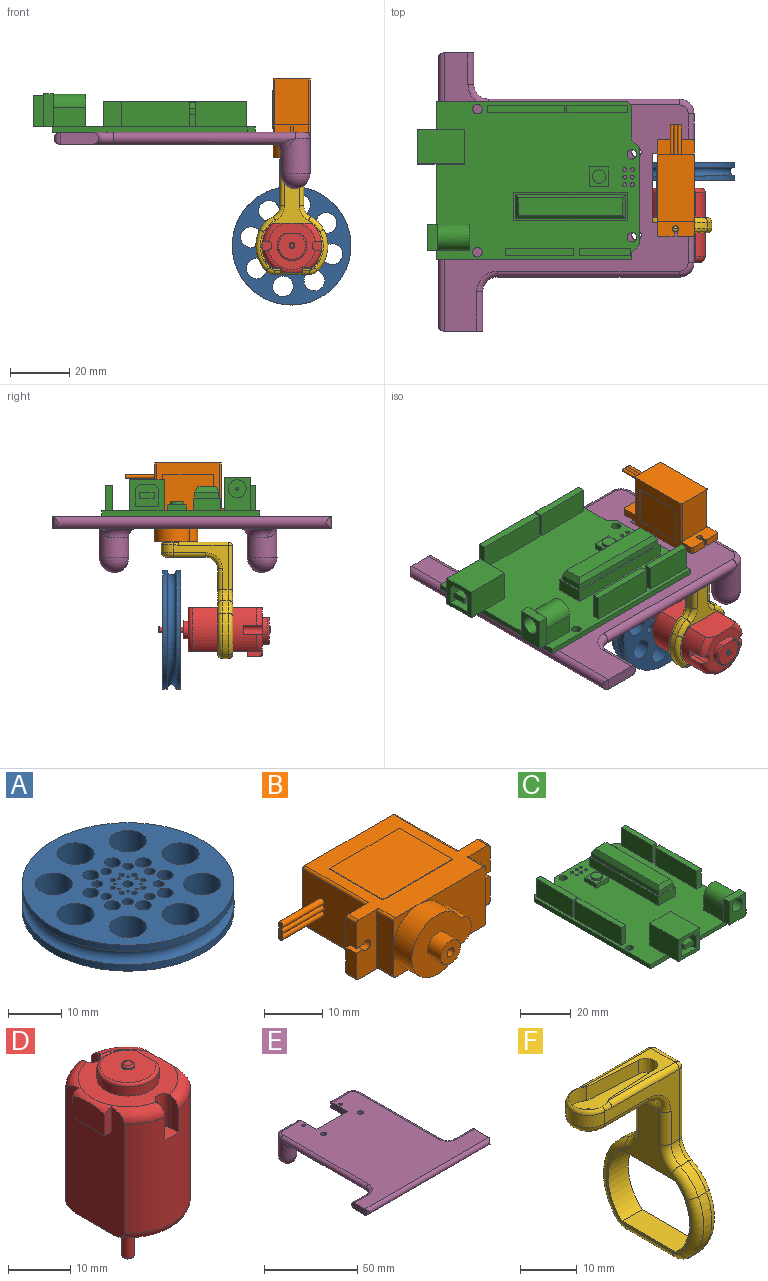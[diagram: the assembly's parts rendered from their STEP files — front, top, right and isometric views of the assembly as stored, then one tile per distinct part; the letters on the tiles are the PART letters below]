
ASSEMBLY  parts=6 mates=5
PART A: 46 faces, bbox 45.6x45.6x6 mm
  f0: cylinder r=20mm len=40mm, axis (0,0,-1), area 188.5mm2, adj f3,f45
  f1: cylinder r=20mm len=40mm, axis (0,0,-1), area 188.5mm2, adj f4,f45
  f2: cylinder r=1mm len=6mm, axis (0,0,-1), area 37.7mm2, adj f3,f4
  f3: plane 40x40mm, normal (0,0,1), area 856.1mm2, adj f0,f2,f5,f6,f7,f8,f9,f10
  f4: plane 40x40mm, normal (0,0,-1), area 856.1mm2, adj f1,f2,f5,f6,f7,f8,f9,f10
  f5: cylinder r=3.5mm len=7mm, axis (0,0,1), area 131.9mm2, adj f3,f4
  f6: cylinder r=3.5mm len=7mm, axis (0,0,1), area 131.9mm2, adj f3,f4
  f7: cylinder r=3.5mm len=7mm, axis (0,0,1), area 131.9mm2, adj f3,f4
  f8: cylinder r=3.5mm len=7mm, axis (0,0,1), area 131.9mm2, adj f3,f4
  f9: cylinder r=3.5mm len=7mm, axis (0,0,1), area 131.9mm2, adj f3,f4
  f10: cylinder r=3.5mm len=7mm, axis (0,0,1), area 131.9mm2, adj f3,f4
  f11: cylinder r=3.5mm len=7mm, axis (0,0,1), area 131.9mm2, adj f3,f4
  f12: cylinder r=3.5mm len=7mm, axis (0,0,1), area 131.9mm2, adj f3,f4
  f13: cylinder r=1.5mm len=6mm, axis (0,0,1), area 56.5mm2, adj f3,f4
  f14: cylinder r=0.5mm len=6mm, axis (0,0,1), area 18.8mm2, adj f3,f4
  f15: cylinder r=0.5mm len=6mm, axis (0,0,1), area 18.8mm2, adj f3,f4
  f16: cylinder r=0.5mm len=6mm, axis (0,0,1), area 18.8mm2, adj f3,f4
  f17: cylinder r=0.5mm len=6mm, axis (0,0,1), area 18.8mm2, adj f3,f4
  f18: cylinder r=0.5mm len=6mm, axis (0,0,1), area 18.8mm2, adj f3,f4
  f19: cylinder r=0.5mm len=6mm, axis (0,0,1), area 18.8mm2, adj f3,f4
  f20: cylinder r=0.5mm len=6mm, axis (0,0,1), area 18.8mm2, adj f3,f4
  f21: cylinder r=0.25mm len=6mm, axis (0,0,1), area 9.4mm2, adj f3,f4
  f22: cylinder r=0.25mm len=6mm, axis (0,0,1), area 9.4mm2, adj f3,f4
  f23: cylinder r=0.25mm len=6mm, axis (0,0,1), area 9.4mm2, adj f3,f4
  f24: cylinder r=0.25mm len=6mm, axis (0,0,1), area 9.4mm2, adj f3,f4
  f25: cylinder r=0.25mm len=6mm, axis (0,0,1), area 9.4mm2, adj f3,f4
  f26: cylinder r=0.25mm len=6mm, axis (0,0,1), area 9.4mm2, adj f3,f4
  f27: cylinder r=0.25mm len=6mm, axis (0,0,1), area 9.4mm2, adj f3,f4
  f28: cylinder r=0.25mm len=6mm, axis (0,0,1), area 9.4mm2, adj f3,f4
  f29: cylinder r=1.5mm len=6mm, axis (0,0,1), area 56.5mm2, adj f3,f4
  f30: cylinder r=1.5mm len=6mm, axis (0,0,1), area 56.5mm2, adj f3,f4
  f31: cylinder r=1.5mm len=6mm, axis (0,0,1), area 56.5mm2, adj f3,f4
  f32: cylinder r=1.5mm len=6mm, axis (0,0,1), area 56.5mm2, adj f3,f4
  f33: cylinder r=1.5mm len=6mm, axis (0,0,1), area 56.5mm2, adj f3,f4
  f34: cylinder r=1.5mm len=6mm, axis (0,0,1), area 56.5mm2, adj f3,f4
  f35: cylinder r=1.5mm len=6mm, axis (0,0,1), area 56.5mm2, adj f3,f4
  f36: cylinder r=1mm len=6mm, axis (0,0,1), area 37.7mm2, adj f3,f4
  f37: cylinder r=0.5mm len=6mm, axis (0,0,1), area 18.8mm2, adj f3,f4
  f38: cylinder r=1mm len=6mm, axis (0,0,1), area 37.7mm2, adj f3,f4
  f39: cylinder r=1mm len=6mm, axis (0,0,1), area 37.7mm2, adj f3,f4
  f40: cylinder r=1mm len=6mm, axis (0,0,1), area 37.7mm2, adj f3,f4
  f41: cylinder r=1mm len=6mm, axis (0,0,1), area 37.7mm2, adj f3,f4
  f42: cylinder r=1mm len=6mm, axis (0,0,1), area 37.7mm2, adj f3,f4
  f43: cylinder r=1mm len=6mm, axis (0,0,1), area 37.7mm2, adj f3,f4
  f44: cylinder r=1mm len=6mm, axis (0,0,1), area 37.7mm2, adj f3,f4
  f45: torus R=20mm, axis (0,0,1), area 563.9mm2, adj f0,f1
PART B: 59 faces, bbox 37.5x29.7x12.7 mm
  f0: plane 31.5x22mm, normal (0,0,-1), area 277mm2, adj f1,f3,f4,f15,f16,f17,f23,f25
  f1: cylinder r=0.5mm len=4mm, axis (0,-1,0), area 3.1mm2, adj f0,f3,f20,f23
  f2: plane 6.25x6.25mm, normal (0,-1,0), area 8.3mm2, adj f5,f7,f18,f47
  f3: plane 16.25x12.5mm, normal (0,-1,0), area 132.6mm2, adj f0,f1,f18,f20,f22,f47,f48
  f4: plane 6.25x6.25mm, normal (0,-1,0), area 8.3mm2, adj f0,f7,f34,f47
  f5: cylinder r=0.5mm len=4mm, axis (0,-1,0), area 3.1mm2, adj f2,f7,f18,f33
  f6: plane 15.5x11.5mm, normal (-1,0,0), area 174.9mm2, adj f8,f12,f13,f14,f15,f16,f17
  f7: plane 11.5x4mm, normal (-1,0,0), area 46mm2, adj f2,f4,f5,f33,f34
  f8: cylinder r=0.6mm len=10mm, axis (-1,0,0), area 37.7mm2, adj f6,f9
  f9: plane 1.2x1.2mm, normal (-1,0,0), area 1.1mm2, adj f8
  f10: plane 1.2x1.2mm, normal (-1,0,0), area 1.1mm2, adj f12
  f11: plane 1.2x1.2mm, normal (-1,0,0), area 1.1mm2, adj f13
  f12: cylinder r=0.6mm len=10mm, axis (-1,0,0), area 37.7mm2, adj f6,f10
  f13: cylinder r=0.6mm len=10mm, axis (-1,0,0), area 37.7mm2, adj f6,f11
  f14: cylinder r=0.5mm len=15.5mm, axis (0,-1,0), area 12.2mm2, adj f6,f15,f17,f18
  f15: plane 22.5x12.5mm, normal (0,1,0), area 281mm2, adj f0,f6,f14,f16,f18,f19,f21,f26
  f16: cylinder r=0.5mm len=15.5mm, axis (0,1,0), area 12.2mm2, adj f0,f6,f15,f17
  f17: plane 12.5x5.5mm, normal (0,1,0), area 57.8mm2, adj f0,f6,f14,f16,f18,f35,f36,f37
  f18: plane 31.5x22mm, normal (0,0,1), area 277mm2, adj f2,f3,f5,f14,f15,f17,f19,f22
  f19: cylinder r=0.5mm len=15.5mm, axis (0,1,0), area 12.2mm2, adj f15,f18,f21,f25
  f20: plane 11.5x4mm, normal (1,0,0), area 46mm2, adj f1,f3,f22,f23
  f21: plane 15.5x11.5mm, normal (1,0,0), area 178.2mm2, adj f15,f19,f25,f26
  f22: cylinder r=0.5mm len=4mm, axis (0,1,0), area 3.1mm2, adj f3,f18,f20,f23
  f23: plane 12.5x5.5mm, normal (0,-1,0), area 57.8mm2, adj f0,f1,f18,f20,f22,f24,f27,f28
  f24: cylinder r=0.5mm len=2.5mm, axis (0,1,0), area 2mm2, adj f18,f23,f25,f28
  f25: plane 12.5x5.5mm, normal (0,1,0), area 57.8mm2, adj f0,f18,f19,f21,f24,f26,f27,f28
  f26: cylinder r=0.5mm len=15.5mm, axis (0,-1,0), area 12.2mm2, adj f0,f15,f21,f25
  f27: cylinder r=0.5mm len=2.5mm, axis (0,-1,0), area 2mm2, adj f0,f23,f25,f29
  f28: plane 5.25x2.5mm, normal (1,0,0), area 13.1mm2, adj f23,f24,f25,f30
  f29: plane 5.25x2.5mm, normal (1,0,0), area 13.1mm2, adj f23,f25,f27,f32
  f30: plane 2.5x1.63mm, normal (0,0,-1), area 4.1mm2, adj f23,f25,f28,f31
  f31: cylinder r=1mm len=2.5mm, axis (0,-1,0), area 13.1mm2, adj f23,f25,f30,f32
  f32: plane 2.5x1.63mm, normal (0,0,1), area 4.1mm2, adj f23,f25,f29,f31
  f33: plane 12.5x5.5mm, normal (0,-1,0), area 57.8mm2, adj f0,f5,f7,f18,f34,f35,f36,f37
  f34: cylinder r=0.5mm len=4mm, axis (0,1,0), area 3.1mm2, adj f0,f4,f7,f33
  f35: cylinder r=0.5mm len=2.5mm, axis (0,1,0), area 2mm2, adj f0,f17,f33,f37
  f36: plane 5.25x2.5mm, normal (-1,0,0), area 13.1mm2, adj f17,f33,f38,f39
  f37: plane 5.25x2.5mm, normal (-1,0,0), area 13.1mm2, adj f17,f33,f35,f41
  f38: cylinder r=0.5mm len=2.5mm, axis (0,-1,0), area 2mm2, adj f17,f18,f33,f36
  f39: plane 2.5x1.63mm, normal (0,0,-1), area 4.1mm2, adj f17,f33,f36,f40
  f40: cylinder r=1mm len=2.5mm, axis (0,-1,0), area 13.1mm2, adj f17,f33,f39,f41
  f41: plane 2.5x1.63mm, normal (0,0,1), area 4.1mm2, adj f17,f33,f37,f40
  f42: plane 13x0.1mm, normal (-1,0,0), area 1.3mm2, adj f18,f43,f45,f46
  f43: plane 17x0.1mm, normal (0,1,0), area 1.7mm2, adj f18,f42,f44,f46
  f44: plane 13x0.1mm, normal (1,0,0), area 1.3mm2, adj f18,f43,f45,f46
  f45: plane 17x0.1mm, normal (0,-1,0), area 1.7mm2, adj f18,f42,f44,f46
  f46: plane 17x13mm, normal (0,0,1), area 221mm2, adj f42,f43,f44,f45
  f47: cylinder r=6.25mm len=12.5mm, axis (0,-1,0), area 150.6mm2, adj f2,f3,f4,f48,f49
  f48: cylinder r=2.8mm len=5.59mm, axis (0,-1,0), area 38.3mm2, adj f3,f47,f49
  f49: plane 14.5x12.5mm, normal (0,-1,0), area 113.7mm2, adj f47,f48,f51
  f50: plane 1.7x1.7mm, normal (0,-1,0), area 2.3mm2, adj f53
  f51: cylinder r=2.4mm len=4.8mm, axis (0,-1,0), area 48.3mm2, adj f49,f52
  f52: plane 4.8x4.8mm, normal (0,-1,0), area 15.8mm2, adj f51,f53
  f53: cylinder r=0.85mm len=3.2mm, axis (0,-1,0), area 17.1mm2, adj f50,f52
  f54: plane 13x0.1mm, normal (-1,0,0), area 1.3mm2, adj f0,f55,f56,f57
  f55: plane 17x0.1mm, normal (0,1,0), area 1.7mm2, adj f0,f54,f56,f58
  f56: plane 17x13mm, normal (0,0,-1), area 221mm2, adj f54,f55,f57,f58
  f57: plane 17x0.1mm, normal (0,-1,0), area 1.7mm2, adj f0,f54,f56,f58
  f58: plane 13x0.1mm, normal (1,0,0), area 1.3mm2, adj f0,f55,f56,f57
PART C: 159 faces, bbox 53.3x75x13 mm
  f0: plane 68.58x53.34mm, normal (0,0,1), area 2744.3mm2, adj f1,f2,f3,f4,f5,f6,f7,f8
  f1: plane 2.54x2.54mm, normal (0.71,0.71,0), area 6.8mm2, adj f0,f2,f51,f52
  f2: plane 32.77x1.9mm, normal (0,1,0), area 62.3mm2, adj f0,f1,f3,f52
  f3: plane 2.54x2.54mm, normal (-0.71,0.71,0), area 6.8mm2, adj f0,f2,f4,f52
  f4: plane 11.43x1.9mm, normal (0,1,0), area 21.7mm2, adj f0,f3,f5,f52
  f5: plane 1.9x1.52mm, normal (-0.71,0.71,0), area 4.1mm2, adj f0,f4,f6,f52
  f6: plane 64.52x1.9mm, normal (-1,0,0), area 122.6mm2, adj f0,f5,f7,f52
  f7: plane 53.34x1.9mm, normal (0,-1,0), area 101.3mm2, adj f0,f6,f8,f52,f81,f99,f107,f108
  f8: plane 66.04x1.9mm, normal (1,0,0), area 125.5mm2, adj f0,f7,f51,f52
  f9: cylinder r=1.59mm len=3.18mm, axis (0,0,-1), area 19mm2, adj f0,f52
  f10: cylinder r=1.59mm len=3.18mm, axis (0,0,-1), area 19mm2, adj f0,f52
  f11: cylinder r=1.59mm len=3.18mm, axis (0,0,-1), area 19mm2, adj f0,f52
  f12: cylinder r=1.59mm len=3.18mm, axis (0,0,-1), area 19mm2, adj f0,f52
  f13: cylinder r=0.64mm len=1.9mm, axis (0,0,-1), area 7.6mm2, adj f52,f80
  f14: cylinder r=0.64mm len=1.9mm, axis (0,0,-1), area 7.6mm2, adj f52,f79
  f15: cylinder r=0.64mm len=1.9mm, axis (0,0,-1), area 7.6mm2, adj f52,f78
  f16: cylinder r=0.64mm len=1.9mm, axis (0,0,-1), area 7.6mm2, adj f52,f77
  f17: cylinder r=0.64mm len=1.9mm, axis (0,0,-1), area 7.6mm2, adj f52,f76
  f18: cylinder r=0.64mm len=1.9mm, axis (0,0,-1), area 7.6mm2, adj f52,f75
  f19: cylinder r=0.64mm len=1.9mm, axis (0,0,-1), area 7.6mm2, adj f52,f74
  f20: cylinder r=0.64mm len=1.9mm, axis (0,0,-1), area 7.6mm2, adj f52,f73
  f21: cylinder r=0.64mm len=1.9mm, axis (0,0,-1), area 7.6mm2, adj f52,f72
  f22: cylinder r=0.64mm len=1.9mm, axis (0,0,-1), area 7.6mm2, adj f52,f71
  f23: cylinder r=0.64mm len=1.9mm, axis (0,0,-1), area 7.6mm2, adj f52,f58
  f24: cylinder r=0.64mm len=1.9mm, axis (0,0,-1), area 7.6mm2, adj f52,f140
  f25: cylinder r=0.64mm len=1.9mm, axis (0,0,-1), area 7.6mm2, adj f52,f151
  f26: cylinder r=0.64mm len=1.9mm, axis (0,0,-1), area 7.6mm2, adj f52,f59
  f27: cylinder r=0.64mm len=1.9mm, axis (0,0,-1), area 7.6mm2, adj f52,f60
  f28: cylinder r=0.64mm len=1.9mm, axis (0,0,-1), area 7.6mm2, adj f52,f61
  f29: cylinder r=0.64mm len=1.9mm, axis (0,0,-1), area 7.6mm2, adj f52,f62
  f30: cylinder r=0.64mm len=1.9mm, axis (0,0,-1), area 7.6mm2, adj f52,f63
  f31: cylinder r=0.64mm len=1.9mm, axis (0,0,-1), area 7.6mm2, adj f52,f64
  f32: cylinder r=0.64mm len=1.9mm, axis (0,0,-1), area 7.6mm2, adj f52,f65
  f33: cylinder r=0.64mm len=1.9mm, axis (0,0,-1), area 7.6mm2, adj f52,f139
  f34: cylinder r=0.64mm len=1.9mm, axis (0,0,-1), area 7.6mm2, adj f52,f138
  f35: cylinder r=0.64mm len=1.9mm, axis (0,0,-1), area 7.6mm2, adj f52,f137
  f36: cylinder r=0.64mm len=1.9mm, axis (0,0,-1), area 7.6mm2, adj f52,f136
  f37: cylinder r=0.64mm len=1.9mm, axis (0,0,-1), area 7.6mm2, adj f52,f135
  f38: cylinder r=0.64mm len=1.9mm, axis (0,0,-1), area 7.6mm2, adj f52,f134
  f39: cylinder r=0.64mm len=1.9mm, axis (0,0,-1), area 7.6mm2, adj f52,f133
  f40: cylinder r=0.64mm len=1.9mm, axis (0,0,-1), area 7.6mm2, adj f52,f150
  f41: cylinder r=0.64mm len=1.9mm, axis (0,0,-1), area 7.6mm2, adj f52,f149
  f42: cylinder r=0.64mm len=1.9mm, axis (0,0,-1), area 7.6mm2, adj f52,f148
  f43: cylinder r=0.64mm len=1.9mm, axis (0,0,-1), area 7.6mm2, adj f52,f147
  f44: cylinder r=0.64mm len=1.9mm, axis (0,0,-1), area 7.6mm2, adj f52,f146
  f45: cylinder r=0.64mm len=1.9mm, axis (0,0,-1), area 7.6mm2, adj f0,f52
  f46: cylinder r=0.64mm len=1.9mm, axis (0,0,-1), area 7.6mm2, adj f0,f52
  f47: cylinder r=0.64mm len=1.9mm, axis (0,0,-1), area 7.6mm2, adj f0,f52
  f48: cylinder r=0.64mm len=1.9mm, axis (0,0,-1), area 7.6mm2, adj f0,f52
  f49: cylinder r=0.64mm len=1.9mm, axis (0,0,-1), area 7.6mm2, adj f0,f52
  f50: cylinder r=0.64mm len=1.9mm, axis (0,0,-1), area 7.6mm2, adj f0,f52
  f51: plane 2.54x1.9mm, normal (0,1,0), area 4.8mm2, adj f0,f1,f8,f52
  f52: plane 68.58x53.34mm, normal (0,0,-1), area 3531.3mm2, adj f1,f2,f3,f4,f5,f6,f7,f8
  f53: plane 20.48x2.5mm, normal (0,0,1), area 51.2mm2, adj f54,f55,f56,f57
  f54: plane 8.6x2.5mm, normal (0,1,0), area 21.5mm2, adj f0,f53,f55,f57
  f55: plane 20.48x8.6mm, normal (1,0,0), area 176.1mm2, adj f0,f53,f54,f56
  f56: plane 8.6x2.5mm, normal (0,-1,0), area 21.5mm2, adj f0,f53,f55,f57
  f57: plane 20.48x8.6mm, normal (-1,0,0), area 176.1mm2, adj f0,f53,f54,f56
  f58: plane 1.27x1.27mm, normal (0,0,-1), area 1.3mm2, adj f23
  f59: plane 1.27x1.27mm, normal (0,0,-1), area 1.3mm2, adj f26
  f60: plane 1.27x1.27mm, normal (0,0,-1), area 1.3mm2, adj f27
  f61: plane 1.27x1.27mm, normal (0,0,-1), area 1.3mm2, adj f28
  f62: plane 1.27x1.27mm, normal (0,0,-1), area 1.3mm2, adj f29
  f63: plane 1.27x1.27mm, normal (0,0,-1), area 1.3mm2, adj f30
  f64: plane 1.27x1.27mm, normal (0,0,-1), area 1.3mm2, adj f31
  f65: plane 1.27x1.27mm, normal (0,0,-1), area 1.3mm2, adj f32
  f66: plane 26x2.5mm, normal (0,0,1), area 65mm2, adj f67,f68,f69,f70
  f67: plane 26x8.6mm, normal (1,0,0), area 223.6mm2, adj f0,f66,f68,f70
  f68: plane 8.6x2.5mm, normal (0,-1,0), area 21.5mm2, adj f0,f66,f67,f69
  f69: plane 26x8.6mm, normal (-1,0,0), area 223.6mm2, adj f0,f66,f68,f70
  f70: plane 8.6x2.5mm, normal (0,1,0), area 21.5mm2, adj f0,f66,f67,f69
  f71: plane 1.27x1.27mm, normal (0,0,-1), area 1.3mm2, adj f22
  f72: plane 1.27x1.27mm, normal (0,0,-1), area 1.3mm2, adj f21
  f73: plane 1.27x1.27mm, normal (0,0,-1), area 1.3mm2, adj f20
  f74: plane 1.27x1.27mm, normal (0,0,-1), area 1.3mm2, adj f19
  f75: plane 1.27x1.27mm, normal (0,0,-1), area 1.3mm2, adj f18
  f76: plane 1.27x1.27mm, normal (0,0,-1), area 1.3mm2, adj f17
  f77: plane 1.27x1.27mm, normal (0,0,-1), area 1.3mm2, adj f16
  f78: plane 1.27x1.27mm, normal (0,0,-1), area 1.3mm2, adj f15
  f79: plane 1.27x1.27mm, normal (0,0,-1), area 1.3mm2, adj f14
  f80: plane 1.27x1.27mm, normal (0,0,-1), area 1.3mm2, adj f13
  f81: plane 11.6x6.38mm, normal (0,0,-1), area 73.9mm2, adj f7,f82,f83,f85
  f82: plane 11.6x10.5mm, normal (0,-1,0), area 64.6mm2, adj f81,f83,f85,f86,f87,f88,f89,f90
  f83: plane 16x10.5mm, normal (1,0,0), area 168mm2, adj f0,f81,f82,f84,f86
  f84: plane 11.6x10.5mm, normal (0,1,0), area 121.8mm2, adj f0,f83,f85,f86
  f85: plane 16x10.5mm, normal (-1,0,0), area 168mm2, adj f0,f81,f82,f84,f86
  f86: plane 16x11.6mm, normal (0,0,1), area 185.6mm2, adj f82,f83,f84,f85
  f87: plane 14.14x5.02mm, normal (0,0,-1), area 71mm2, adj f82,f88,f92,f93
  f88: plane 14.14x1.44mm, normal (0.71,0,-0.71), area 28.8mm2, adj f82,f87,f89,f93
  f89: plane 14.14x6.06mm, normal (1,0,0), area 85.7mm2, adj f82,f88,f90,f93
  f90: plane 14.14x7.9mm, normal (0,0,1), area 111.7mm2, adj f82,f89,f91,f93
  f91: plane 14.14x6.06mm, normal (-1,0,0), area 85.7mm2, adj f82,f90,f92,f93
  f92: plane 14.14x1.44mm, normal (-0.71,0,-0.71), area 28.8mm2, adj f82,f87,f91,f93
  f93: plane 7.9x7.5mm, normal (0,-1,0), area 47mm2, adj f87,f88,f89,f90,f91,f92,f95,f96
  f94: plane 4.88x2.08mm, normal (0,-1,0), area 10.2mm2, adj f95,f96,f97,f98
  f95: plane 14.14x4.88mm, normal (0,0,1), area 69mm2, adj f93,f94,f96,f98
  f96: plane 14.14x2.08mm, normal (-1,0,0), area 29.4mm2, adj f93,f94,f95,f97
  f97: plane 14.14x4.88mm, normal (0,0,-1), area 69mm2, adj f93,f94,f96,f98
  f98: plane 14.14x2.08mm, normal (1,0,0), area 29.4mm2, adj f93,f94,f95,f97
  f99: plane 8.88x2.88mm, normal (0,0,-1), area 25.5mm2, adj f7,f107,f108,f109
  f100: plane 11x6.49mm, normal (1,0,0), area 71.4mm2, adj f0,f101,f103,f104
  f101: cylinder r=4.44mm len=11mm, axis (0,-1,0), area 153.4mm2, adj f100,f102,f103,f104,f105
  f102: plane 11x6.49mm, normal (-1,0,0), area 71.4mm2, adj f0,f101,f103,f105
  f103: plane 10.93x8.88mm, normal (0,1,0), area 88.6mm2, adj f0,f100,f101,f102
  f104: plane 6.63x0mm, normal (0,-1,0), area 0mm2, adj f0,f100,f101,f108
  f105: plane 11.12x8.88mm, normal (0,1,0), area 10.1mm2, adj f0,f101,f102,f106,f107,f108
  f106: plane 8.88x3.3mm, normal (0,0,1), area 29.3mm2, adj f105,f107,f108,f109
  f107: plane 11.13x3.3mm, normal (-1,0,0), area 36.7mm2, adj f0,f7,f99,f105,f106,f109
  f108: plane 11.13x3.3mm, normal (1,0,0), area 36.7mm2, adj f0,f7,f99,f104,f105,f106,f109
  f109: plane 11.13x8.88mm, normal (0,-1,0), area 70.5mm2, adj f99,f106,f107,f108,f110
  f110: cylinder r=3mm len=12.8mm, axis (0,-1,0), area 241.3mm2, adj f109,f111
  f111: plane 6x6mm, normal (0,-1,0), area 27.5mm2, adj f110,f112
  f112: cylinder r=0.5mm len=10mm, axis (0,1,0), area 31.4mm2, adj f111,f113
  f113: sphere r=0.5mm, area 1.6mm2, adj f112
  f114: plane 9.33x4.3mm, normal (0,-1,0), area 40.1mm2, adj f0,f115,f117,f118
  f115: plane 38.37x4.3mm, normal (1,0,0), area 164.8mm2, adj f0,f114,f116,f118
  f116: plane 9.33x4.3mm, normal (0,1,0), area 40.1mm2, adj f0,f115,f117,f118
  f117: plane 38.37x4.3mm, normal (-1,0,0), area 164.8mm2, adj f0,f114,f116,f118
  f118: plane 38.37x9.33mm, normal (0,0,1), area 57.4mm2, adj f114,f115,f116,f117,f119,f120,f121,f122
  f119: plane 37.19x2mm, normal (-1,0,0), area 74.4mm2, adj f118,f120,f122,f127
  f120: plane 8.08x2mm, normal (0,-1,0), area 16.2mm2, adj f118,f119,f121,f126
  f121: plane 37.19x2mm, normal (1,0,0), area 74.4mm2, adj f118,f120,f122,f125
  f122: plane 8.08x2mm, normal (0,1,0), area 16.2mm2, adj f118,f119,f121,f124
  f123: plane 35.16x6.05mm, normal (0,0,1), area 212.7mm2, adj f124,f125,f126,f127
  f124: plane 8.08x2mm, normal (0,0.9,0.44), area 15.7mm2, adj f122,f123,f125,f127
  f125: plane 37.19x2mm, normal (0.89,0,0.45), area 81.1mm2, adj f121,f123,f124,f126
  f126: plane 8.08x2mm, normal (0,-0.88,0.47), area 16mm2, adj f120,f123,f125,f127
  f127: plane 37.19x2mm, normal (-0.89,0,0.45), area 81.2mm2, adj f119,f123,f124,f126
  f128: plane 23x2.44mm, normal (0,0,1), area 56mm2, adj f129,f130,f131,f132
  f129: plane 23x8.6mm, normal (1,0,0), area 197.8mm2, adj f0,f128,f130,f132
  f130: plane 8.6x2.44mm, normal (0,-1,0), area 20.9mm2, adj f0,f128,f129,f131
  f131: plane 23x8.6mm, normal (-1,0,0), area 197.8mm2, adj f0,f128,f130,f132
  f132: plane 8.6x2.44mm, normal (0,1,0), area 20.9mm2, adj f0,f128,f129,f131
  f133: plane 1.27x1.27mm, normal (0,0,-1), area 1.3mm2, adj f39
  f134: plane 1.27x1.27mm, normal (0,0,-1), area 1.3mm2, adj f38
  f135: plane 1.27x1.27mm, normal (0,0,-1), area 1.3mm2, adj f37
  f136: plane 1.27x1.27mm, normal (0,0,-1), area 1.3mm2, adj f36
  f137: plane 1.27x1.27mm, normal (0,0,-1), area 1.3mm2, adj f35
  f138: plane 1.27x1.27mm, normal (0,0,-1), area 1.3mm2, adj f34
  f139: plane 1.27x1.27mm, normal (0,0,-1), area 1.3mm2, adj f33
  f140: plane 1.27x1.27mm, normal (0,0,-1), area 1.3mm2, adj f24
  f141: plane 17.27x2.44mm, normal (0,0,1), area 42.1mm2, adj f142,f143,f144,f145
  f142: plane 8.6x2.44mm, normal (0,-1,0), area 20.9mm2, adj f0,f141,f143,f145
  f143: plane 17.27x8.6mm, normal (-1,0,0), area 148.6mm2, adj f0,f141,f142,f144
  f144: plane 8.6x2.44mm, normal (0,1,0), area 20.9mm2, adj f0,f141,f143,f145
  f145: plane 17.27x8.6mm, normal (1,0,0), area 148.6mm2, adj f0,f141,f142,f144
  f146: plane 1.27x1.27mm, normal (0,0,-1), area 1.3mm2, adj f44
  f147: plane 1.27x1.27mm, normal (0,0,-1), area 1.3mm2, adj f43
  f148: plane 1.27x1.27mm, normal (0,0,-1), area 1.3mm2, adj f42
  f149: plane 1.27x1.27mm, normal (0,0,-1), area 1.3mm2, adj f41
  f150: plane 1.27x1.27mm, normal (0,0,-1), area 1.3mm2, adj f40
  f151: plane 1.27x1.27mm, normal (0,0,-1), area 1.3mm2, adj f25
  f152: plane 6.5x2mm, normal (-1,0,0), area 13mm2, adj f0,f153,f155,f156
  f153: plane 6.5x2mm, normal (0,-1,0), area 13mm2, adj f0,f152,f154,f156
  f154: plane 6.5x2mm, normal (1,0,0), area 13mm2, adj f0,f153,f155,f156
  f155: plane 6.5x2mm, normal (0,1,0), area 13mm2, adj f0,f152,f154,f156
  f156: plane 6.5x6.5mm, normal (0,0,1), area 26.4mm2, adj f152,f153,f154,f155,f157
  f157: cylinder r=2.24mm len=4.49mm, axis (0,0,-1), area 14.1mm2, adj f156,f158
  f158: plane 4.49x4.49mm, normal (0,0,1), area 15.8mm2, adj f157
PART D: 35 faces, bbox 21.1x21.8x38 mm
  f0: plane 15.74x15.5mm, normal (0,0,1), area 119.4mm2, adj f4,f10,f11,f22,f26,f29,f30,f31
  f1: cylinder r=10mm len=21.5mm, axis (0,0,-1), area 351.1mm2, adj f4,f5,f23,f24,f25,f27,f29,f30
  f2: plane 17x15mm, normal (0,0,-1), area 187.9mm2, adj f4,f5,f6,f27,f28
  f3: cylinder r=10mm len=21.5mm, axis (0,0,-1), area 351.1mm2, adj f4,f5,f19,f20,f21,f28,f30,f31
  f4: plane 25x13.23mm, normal (1,0,0), area 326.4mm2, adj f0,f1,f2,f3,f27,f28,f29,f31
  f5: plane 24.97x13.23mm, normal (-1,0,0), area 289.4mm2, adj f1,f2,f3,f15,f17,f18,f27,f28
  f6: cylinder r=3mm len=6mm, axis (0,0,1), area 28.3mm2, adj f2,f7
  f7: plane 6x6mm, normal (0,0,-1), area 25.1mm2, adj f6,f8
  f8: cylinder r=1mm len=8.2mm, axis (0,0,1), area 51.5mm2, adj f7,f33
  f9: plane 1.4x1.4mm, normal (0,0,-1), area 1.5mm2, adj f33
  f10: plane 6x2.3mm, normal (1,0,0), area 13.6mm2, adj f0,f11,f12,f34
  f11: cylinder r=5mm len=10mm, axis (0,0,-1), area 45mm2, adj f0,f10,f34
  f12: plane 9x8.5mm, normal (0,0,1), area 59.1mm2, adj f10,f13,f34
  f13: cylinder r=1mm len=2mm, axis (0,0,-1), area 1.9mm2, adj f12,f32
  f14: plane 1.4x1.4mm, normal (0,0,1), area 1.5mm2, adj f32
  f15: plane 5.11x1.64mm, normal (0,1,0), area 7mm2, adj f5,f16,f18,f30
  f16: plane 7.4x4.73mm, normal (-1,0,0), area 33.6mm2, adj f15,f17,f18,f30
  f17: plane 5.11x1.64mm, normal (0,-1,0), area 7mm2, adj f5,f16,f18,f30
  f18: plane 7.4x1.5mm, normal (0,0,-1), area 11.1mm2, adj f5,f15,f16,f17
  f19: plane 6.6x1.78mm, normal (-1,0,0), area 9.8mm2, adj f3,f21,f22,f31
  f20: plane 6.6x1.78mm, normal (1,0,0), area 9.8mm2, adj f3,f21,f22,f30
  f21: plane 3.25x3mm, normal (0,0,1), area 8.7mm2, adj f3,f19,f20,f22
  f22: cylinder r=1.5mm len=6.5mm, axis (0,0,1), area 30.6mm2, adj f0,f19,f20,f21,f30,f31
  f23: plane 6.6x1.78mm, normal (1,0,0), area 9.8mm2, adj f1,f25,f26,f30
  f24: plane 6.6x1.78mm, normal (-1,0,0), area 9.8mm2, adj f1,f25,f26,f29
  f25: plane 3.25x3mm, normal (0,0,1), area 8.7mm2, adj f1,f23,f24,f26
  f26: cylinder r=1.5mm len=6.5mm, axis (0,0,1), area 30.6mm2, adj f0,f23,f24,f25,f29,f30
  f27: torus R=8.5mm, axis (0,0,1), area 41mm2, adj f1,f2,f4,f5
  f28: torus R=8.5mm, axis (0,0,1), area 41mm2, adj f2,f3,f4,f5
  f29: torus R=8mm, axis (0,0,1), area 22.8mm2, adj f0,f1,f4,f24,f26
  f30: torus R=8mm, axis (0,0,1), area 55.9mm2, adj f0,f1,f3,f5,f15,f16,f17,f20
  f31: torus R=8mm, axis (0,0,1), area 22.8mm2, adj f0,f3,f4,f19,f22
  f32: torus R=0.7mm, axis (0,0,1), area 2.6mm2, adj f13,f14
  f33: torus R=0.7mm, axis (0,0,-1), area 2.6mm2, adj f8,f9
  f34: torus R=4.5mm, axis (0,0,1), area 19.3mm2, adj f10,f11,f12
PART E: 36 faces, bbox 93.8x86.7x19 mm
  f0: plane 93.76x82.29mm, normal (0,0,-1), area 4476.7mm2, adj f1,f2,f3,f4,f5,f6,f7,f11
  f1: plane 13x4mm, normal (1,0,0), area 50.3mm2, adj f0,f8,f20,f27
  f2: plane 12x4mm, normal (-1,0,0), area 48mm2, adj f0,f3,f8,f15
  f3: plane 23.5x4mm, normal (0,1,0), area 94mm2, adj f0,f2,f4,f8
  f4: plane 12x4mm, normal (1,0,0), area 48mm2, adj f0,f3,f8,f22
  f5: cylinder r=1mm len=4mm, axis (0,0,-1), area 25.1mm2, adj f0,f8
  f6: plane 10.06x4mm, normal (-1,0,0), area 38.5mm2, adj f0,f8,f26,f29
  f7: cylinder r=1mm len=4mm, axis (0,0,-1), area 25.1mm2, adj f0,f8
  f8: plane 93.76x82.29mm, normal (0,0,1), area 4685.1mm2, adj f1,f2,f3,f4,f5,f6,f7,f11
  f9: cylinder r=5mm len=12mm, axis (0,0,-1), area 281.4mm2, adj f14,f17,f30,f31,f32
  f10: cylinder r=5mm len=12mm, axis (0,0,1), area 281.4mm2, adj f13,f24,f33,f34,f35
  f11: cylinder r=1.59mm len=4mm, axis (0,0,1), area 39.9mm2, adj f0,f8
  f12: cylinder r=1.59mm len=4mm, axis (0,0,1), area 39.9mm2, adj f0,f8
  f13: sphere r=5mm, area 157.1mm2, adj f10
  f14: sphere r=5mm, area 157.1mm2, adj f9
  f15: cylinder r=2mm len=4mm, axis (0,0,1), area 8mm2, adj f2,f16
  f16: cylinder r=2mm len=13.25mm, axis (-1,0,0), area 65.2mm2, adj f0,f8,f15,f17,f30
  f17: torus R=3mm, axis (0,0,1), area 21.1mm2, adj f8,f9,f16,f18
  f18: cylinder r=2mm len=61.29mm, axis (0,1,0), area 371.6mm2, adj f0,f8,f17,f19,f32
  f19: torus R=7mm, axis (0,0,1), area 56.5mm2, adj f0,f8,f18,f20
  f20: cylinder r=2mm len=13.21mm, axis (-1,0,0), area 83mm2, adj f0,f1,f8,f19
  f21: cylinder r=2mm len=13.25mm, axis (-1,0,0), area 65.2mm2, adj f0,f8,f22,f24,f33
  f22: cylinder r=2mm len=4mm, axis (0,0,-1), area 8mm2, adj f4,f21
  f23: cylinder r=2mm len=64.24mm, axis (0,-1,0), area 390.1mm2, adj f0,f8,f24,f25,f35
  f24: torus R=3mm, axis (0,0,1), area 21.1mm2, adj f8,f10,f21,f23
  f25: torus R=7mm, axis (0,0,1), area 56.5mm2, adj f0,f8,f23,f26
  f26: cylinder r=2mm len=10.56mm, axis (-1,0,0), area 66.3mm2, adj f0,f6,f8,f25
  f27: cylinder r=2mm len=4mm, axis (0,0,-1), area 8mm2, adj f1,f28
  f28: cylinder r=2mm len=93.76mm, axis (-1,0,0), area 580mm2, adj f0,f8,f27,f29
  f29: cylinder r=2mm len=4mm, axis (0,0,1), area 8mm2, adj f6,f28
  f30: bspline ~7.73x5mm, area 16.9mm2, adj f9,f16,f31
  f31: torus R=8mm, axis (0,0,1), area 67.1mm2, adj f0,f9,f30,f32
  f32: bspline ~7.73x5mm, area 16.9mm2, adj f9,f18,f31
  f33: bspline ~7.73x5mm, area 16.9mm2, adj f10,f21,f34
  f34: torus R=8mm, axis (0,0,1), area 67.1mm2, adj f0,f10,f33,f35
  f35: bspline ~7.73x5mm, area 16.9mm2, adj f10,f23,f34
PART F: 62 faces, bbox 24.3x26.2x39.9 mm
  f0: cylinder r=12.12mm len=14mm, axis (-1,0,0), area 30.2mm2, adj f23,f25,f39,f52
  f1: plane 11.73x2mm, normal (0,0,-1), area 23.5mm2, adj f25,f26,f42,f53
  f2: cylinder r=12.12mm len=14mm, axis (-1,0,0), area 30.2mm2, adj f24,f26,f38,f49
  f3: plane 18.5x15.18mm, normal (0,1,0), area 78mm2, adj f14,f15,f28,f30,f32,f43,f60,f61
  f4: plane 16.7x6mm, normal (0,0,1), area 35.3mm2, adj f17,f18,f19,f20,f44,f56,f61
  f5: cylinder r=10.12mm len=15.25mm, axis (-1,0,0), area 86.3mm2, adj f6,f8,f10,f11
  f6: plane 13.32x5mm, normal (0,0,1), area 66.6mm2, adj f5,f7,f10,f11
  f7: cylinder r=10.12mm len=15.25mm, axis (-1,0,0), area 86.3mm2, adj f6,f8,f10,f11
  f8: plane 13.32x5mm, normal (0,0,-1), area 66.6mm2, adj f5,f7,f10,f11
  f9: plane 18.5x15.18mm, normal (0,-1,0), area 78mm2, adj f14,f16,f29,f31,f33,f46,f56,f57
  f10: plane 36.25x21.25mm, normal (1,0,0), area 142.8mm2, adj f5,f6,f7,f8,f43,f44,f45,f46
  f11: plane 28.75x21.25mm, normal (-1,0,0), area 105.3mm2, adj f5,f6,f7,f8,f13,f32,f33,f34
  f12: plane 13.5x5mm, normal (0,0,-1), area 61.7mm2, adj f13,f22,f27,f28,f29
  f13: cylinder r=4mm len=5mm, axis (0,1,0), area 31.4mm2, adj f11,f12,f30,f31
  f14: cylinder r=4mm len=8mm, axis (0,0,-1), area 33.1mm2, adj f3,f9,f27,f58
  f15: cylinder r=4mm len=3.6mm, axis (-1,0,0), area 8.9mm2, adj f3,f24,f34,f45
  f16: cylinder r=4mm len=3.6mm, axis (-1,0,0), area 8.9mm2, adj f9,f23,f35,f48
  f17: plane 12.1x3mm, normal (-0.05,-1,0), area 36.4mm2, adj f4,f18,f20,f21
  f18: cylinder r=3.5mm len=7mm, axis (0,0,1), area 47.9mm2, adj f4,f17,f19,f21,f57,f58,f60
  f19: plane 12.1x3mm, normal (-0.05,1,0), area 36.4mm2, adj f4,f18,f20,f21
  f20: cylinder r=2mm len=4mm, axis (0,0,1), area 18.2mm2, adj f4,f17,f19,f21
  f21: plane 19.79x7mm, normal (0,0,1), area 93mm2, adj f17,f18,f19,f20,f22
  f22: cylinder r=1mm len=2mm, axis (0,0,1), area 12.6mm2, adj f12,f21
  f23: cylinder r=10mm len=4.5mm, axis (1,0,0), area 12.8mm2, adj f0,f16,f37,f50
  f24: cylinder r=10mm len=4.5mm, axis (1,0,0), area 12.8mm2, adj f2,f15,f36,f47
  f25: cylinder r=4mm len=2.89mm, axis (-1,0,0), area 6.4mm2, adj f0,f1,f41,f54
  f26: cylinder r=4mm len=2.89mm, axis (-1,0,0), area 6.4mm2, adj f1,f2,f40,f51
  f27: torus R=2.5mm, axis (0,0,-1), area 25.6mm2, adj f12,f14,f28,f29
  f28: cylinder r=1.5mm len=11mm, axis (-1,0,0), area 25.9mm2, adj f3,f12,f27,f30
  f29: cylinder r=1.5mm len=11mm, axis (1,0,0), area 25.9mm2, adj f9,f12,f27,f31
  f30: torus R=5.5mm, axis (0,-1,0), area 16.8mm2, adj f3,f13,f28,f32
  f31: torus R=5.5mm, axis (0,-1,0), area 16.8mm2, adj f9,f13,f29,f33
  f32: cylinder r=1.5mm len=7.05mm, axis (0,0,1), area 16.6mm2, adj f3,f11,f30,f34
  f33: cylinder r=1.5mm len=7.05mm, axis (0,0,-1), area 16.6mm2, adj f9,f11,f31,f35
  f34: torus R=5.5mm, axis (1,0,0), area 12mm2, adj f11,f15,f32,f36
  f35: torus R=5.5mm, axis (1,0,0), area 12mm2, adj f11,f16,f33,f37
  f36: torus R=8.5mm, axis (1,0,0), area 14.2mm2, adj f11,f24,f34,f38
  f37: torus R=8.5mm, axis (1,0,0), area 14.2mm2, adj f11,f23,f35,f39
  f38: torus R=10.62mm, axis (1,0,0), area 34mm2, adj f2,f11,f36,f40
  f39: torus R=10.62mm, axis (1,0,0), area 34mm2, adj f0,f11,f37,f41
  f40: torus R=2.5mm, axis (1,0,0), area 6.6mm2, adj f11,f26,f38,f42
  f41: torus R=2.5mm, axis (1,0,0), area 6.6mm2, adj f11,f25,f39,f42
  f42: cylinder r=1.5mm len=11.73mm, axis (0,1,0), area 27.6mm2, adj f1,f11,f40,f41
  f43: cylinder r=1.5mm len=15.05mm, axis (0,0,-1), area 34.9mm2, adj f3,f10,f45,f59
  f44: cylinder r=1.5mm len=6mm, axis (0,1,0), area 13mm2, adj f4,f10,f55,f59
  f45: torus R=5.5mm, axis (1,0,0), area 12mm2, adj f10,f15,f43,f47
  f46: cylinder r=1.5mm len=15.05mm, axis (0,0,1), area 34.9mm2, adj f9,f10,f48,f55
  f47: torus R=8.5mm, axis (1,0,0), area 14.2mm2, adj f10,f24,f45,f49
  f48: torus R=5.5mm, axis (1,0,0), area 12mm2, adj f10,f16,f46,f50
  f49: torus R=10.62mm, axis (1,0,0), area 34mm2, adj f2,f10,f47,f51
  f50: torus R=8.5mm, axis (1,0,0), area 14.2mm2, adj f10,f23,f48,f52
  f51: torus R=2.5mm, axis (1,0,0), area 6.6mm2, adj f10,f26,f49,f53
  f52: torus R=10.62mm, axis (1,0,0), area 34mm2, adj f0,f10,f50,f54
  f53: cylinder r=1.5mm len=11.73mm, axis (0,-1,0), area 27.6mm2, adj f1,f10,f51,f54
  f54: torus R=2.5mm, axis (1,0,0), area 6.6mm2, adj f10,f25,f52,f53
  f55: bspline ~1.82x1.5mm, area 2.4mm2, adj f44,f46,f56
  f56: cylinder r=1mm len=16.7mm, axis (-1,0,0), area 26.2mm2, adj f4,f9,f55,f57
  f57: bspline ~2.53x1.28mm, area 2.2mm2, adj f9,f18,f56,f58
  f58: torus R=3mm, axis (0,0,1), area 12.6mm2, adj f14,f18,f57,f60
  f59: bspline ~1.82x1.5mm, area 2.4mm2, adj f43,f44,f61
  f60: bspline ~2.91x1.28mm, area 2.2mm2, adj f3,f18,f58,f61
  f61: cylinder r=1mm len=16.7mm, axis (1,0,0), area 26.2mm2, adj f3,f4,f59,f60
PLACE A rot(axis=(0.36,-0.66,0.66),140.9deg) t=(-2.55,18.33,-6.94)mm
PLACE B rot(axis=(0.58,-0.58,-0.58),120deg) t=(3.71,9.77,31.26)mm
PLACE C rot(axis=(0,0,-1),90deg) t=(-50.27,12.24,31.26)mm
PLACE D rot(axis=(0.58,-0.58,0.58),120.2deg) t=(-2.51,9.73,-6.94)mm
PLACE E rot(axis=(0,0,-1),90deg) t=(-39.43,9.77,27.26)mm fixed
PLACE F rot(axis=(0,0,-1),89.7deg) t=(-2.47,-0.23,-7.07)mm
MATE revolute B.f47 <-> F.f18  axis (0,0,-1) through (-2.54,14.77,19.56)mm
MATE fastened E.f7 <-> B.f31  axis (0,0,1) through (-2.54,-3.98,31.26)mm
MATE fastened F.f8 <-> D.f4  axis (0,0,-1) through (-2.45,-2.73,0.56)mm
MATE fastened C.f52 <-> E.f8  axis (0,0,-1) through (-49.66,12.08,31.26)mm
MATE revolute A.f2 <-> D.f8  axis (0,1,0) through (-2.54,15.33,-6.94)mm
